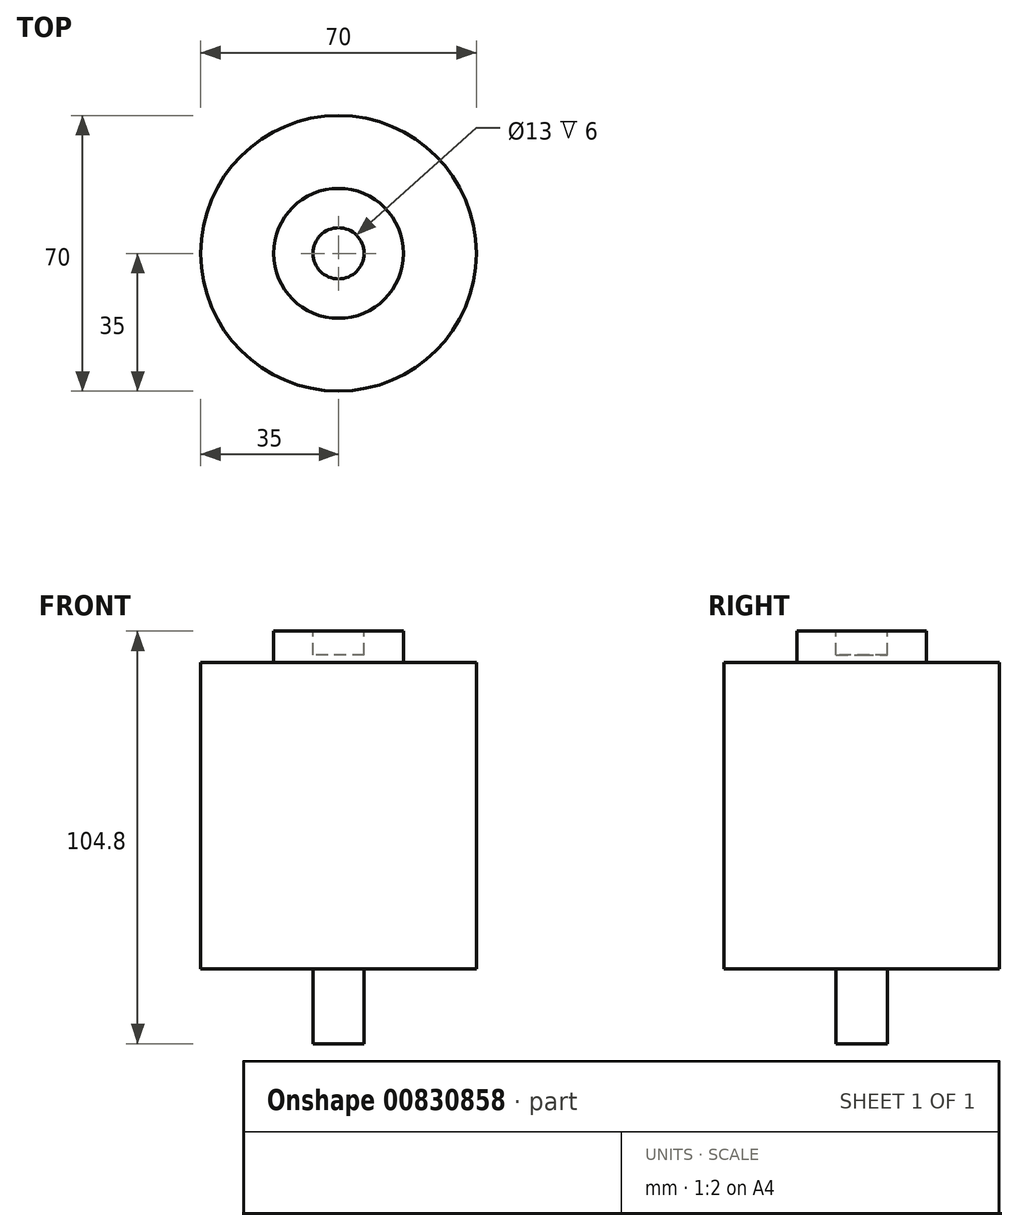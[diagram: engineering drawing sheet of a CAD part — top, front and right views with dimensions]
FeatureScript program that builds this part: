
annotation { "Feature Type Name" : "Feature", "Feature Type Description" : "" }
export const myFeature = defineFeature(function(context is Context, id is Id, definition is map)
    precondition{}
    {
        {
            var Q0;
            Q0=qCreatedBy(makeId("Top.planeOp"),FACE);
            var sketch = newSketch(context, id + "F0", { "sketchPlane" : qUnion([Q0])});
            skCircle(sketch, "E0", {"center": v(0, 0) * mm, "radius": 35 * mm});
            skSolve(sketch);
        }
        {
            var Q0;
            Q0=makeQuery(id+"F0.imprint","IMPRINT",FACE,{"disambiguationData":[TD([[makeQuery(id+"F0.imprint","IMPRINT",EDGE,{"derivedFrom":sQuery(id+"F0.wireOp",EDGE,"E0")}),1.0]])]});
            extrude(context, id + "F1", {"entities" : qUnion([Q0]), "depth" : 77.8 * mm, "offsetDistance" : 25 * mm});
        }
        {
            var Q0;
            Q0=makeQuery(id+"F1.opExtrude","CAP_FACE",FACE,{"disambiguationData":[OSD([sQuery(id+"F0.wireOp",EDGE,"E0")])],"isStart":false});
            var sketch = newSketch(context, id + "F2", { "sketchPlane" : qUnion([Q0])});
            skCircle(sketch, "E1", {"center": v(0, 0) * mm, "radius": 16.5 * mm});
            skSolve(sketch);
        }
        {
            var Q0;
            Q0 = qSketchRegion(id + "F2", true);
            extrude(context, id + "F3", {"entities" : qUnion([Q0]), "depth" : 8 * mm, "offsetDistance" : 25 * mm});
        }
        {
            var Q0;
            Q0=makeQuery(id+"F3.opExtrude","CAP_FACE",FACE,{"disambiguationData":[OSD([sQuery(id+"F2.wireOp",EDGE,"E1")])],"isStart":false});
            var sketch = newSketch(context, id + "F4", { "sketchPlane" : qUnion([Q0])});
            skCircle(sketch, "E2", {"center": v(0, 0) * mm, "radius": 6.5 * mm});
            skSolve(sketch);
        }
        {
            var Q0;
            Q0 = qSketchRegion(id + "F4", true);
            extrude(context, id + "F5", {"entities" : qUnion([Q0]), "operationType" : NewBodyOperationType.REMOVE, "oppositeDirection" : true, "depth" : 6 * mm, "offsetDistance" : 25 * mm});
        }
        {
            var Q0;
            Q0=makeQuery(id+"F1.opExtrude","CAP_FACE",FACE,{"disambiguationData":[OSD([sQuery(id+"F0.wireOp",EDGE,"E0")])],"isStart":true});
            var sketch = newSketch(context, id + "F6", { "sketchPlane" : qUnion([Q0])});
            skCircle(sketch, "E3", {"center": v(0, 0) * mm, "radius": 6.5 * mm});
            skSolve(sketch);
        }
        {
            var Q0;
            Q0 = qSketchRegion(id + "F6", true);
            extrude(context, id + "F7", {"entities" : qUnion([Q0]), "depth" : 19 * mm, "offsetDistance" : 25 * mm});
        }
    });
